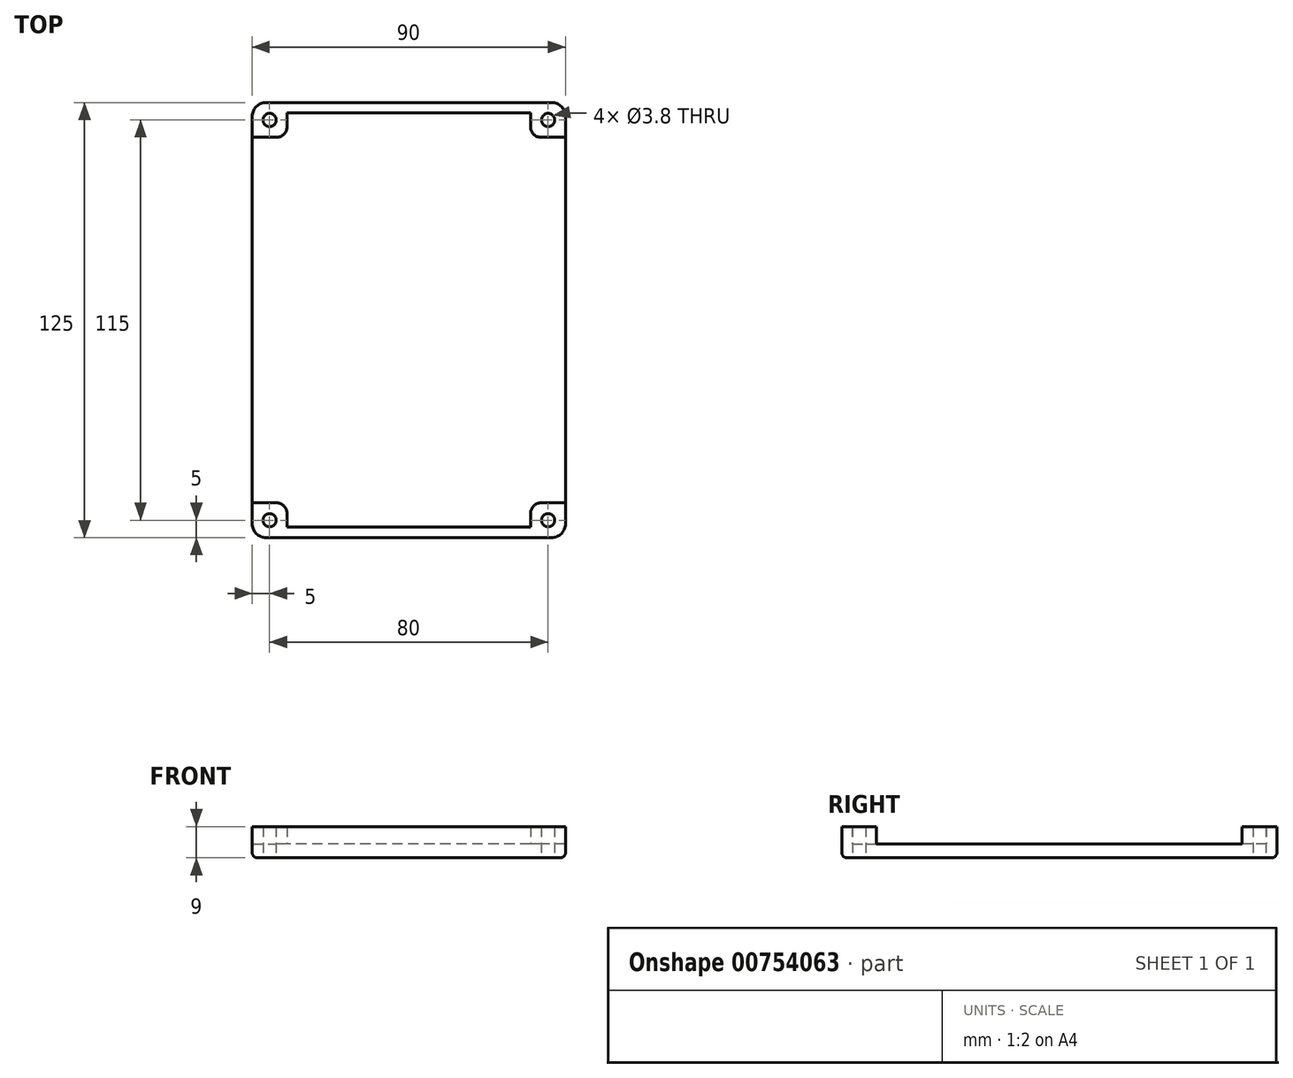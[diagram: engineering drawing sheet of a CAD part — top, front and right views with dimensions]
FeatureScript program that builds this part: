
annotation { "Feature Type Name" : "Feature", "Feature Type Description" : "" }
export const myFeature = defineFeature(function(context is Context, id is Id, definition is map)
    precondition{}
    {
        {
            var Q0;
            Q0=qCreatedBy(makeId("Top.planeOp"),FACE);
            var sketch = newSketch(context, id + "F0", { "sketchPlane" : qUnion([Q0])});
            skLineSegment(sketch, "E0.bottom", {"start": v(-41, 62.5) * mm, "end": v(41, 62.5) * mm});
            skLineSegment(sketch, "E0.top", {"start": v(-41, -62.5) * mm, "end": v(41, -62.5) * mm});
            skLineSegment(sketch, "E0.left", {"start": v(-45, 58.5) * mm, "end": v(-45, -58.5) * mm});
            skLineSegment(sketch, "E0.right", {"start": v(45, 58.5) * mm, "end": v(45, -58.5) * mm});
            skPoint(sketch, "E1.visualSharp", {"position": v(-45, 62.5) * mm});
            skArc(sketch, "E1.filletArc", {"start": v(-41, 62.5) * mm, "mid": v(-43.83, 61.33) * mm, "end": v(-45, 58.5) * mm});
            skPoint(sketch, "E2.visualSharp", {"position": v(45, 62.5) * mm});
            skArc(sketch, "E2.filletArc", {"start": v(45, 58.5) * mm, "mid": v(43.83, 61.33) * mm, "end": v(41, 62.5) * mm});
            skPoint(sketch, "E3.visualSharp", {"position": v(45, -62.5) * mm});
            skArc(sketch, "E3.filletArc", {"start": v(41, -62.5) * mm, "mid": v(43.83, -61.33) * mm, "end": v(45, -58.5) * mm});
            skPoint(sketch, "E4.visualSharp", {"position": v(-45, -62.5) * mm});
            skArc(sketch, "E4.filletArc", {"start": v(-45, -58.5) * mm, "mid": v(-43.83, -61.33) * mm, "end": v(-41, -62.5) * mm});
            skSolve(sketch);
        }
        {
            var Q0;
            Q0 = qSketchRegion(id + "F0", true);
            extrude(context, id + "F1", {"entities" : qUnion([Q0]), "depth" : 4 * mm, "offsetDistance" : 25 * mm});
        }
        {
            var Q0;
            Q0=makeQuery(id+"F1.opExtrude","CAP_FACE",FACE,{"disambiguationData":[OSD([sQuery(id+"F0.wireOp",EDGE,"E0.bottom"),sQuery(id+"F0.wireOp",EDGE,"E0.top"),sQuery(id+"F0.wireOp",EDGE,"E0.left"),sQuery(id+"F0.wireOp",EDGE,"E0.right"),sQuery(id+"F0.wireOp",EDGE,"E1.filletArc"),sQuery(id+"F0.wireOp",EDGE,"E2.filletArc"),sQuery(id+"F0.wireOp",EDGE,"E3.filletArc"),sQuery(id+"F0.wireOp",EDGE,"E4.filletArc")])],"isStart":false});
            var sketch = newSketch(context, id + "F2", { "sketchPlane" : qUnion([Q0])});
            skLineSegment(sketch, "E5.bottom", {"start": v(-41, 62.5) * mm, "end": v(-45, 62.5) * mm, "construction": true});
            skLineSegment(sketch, "E5.top", {"start": v(-41, 58.5) * mm, "end": v(-45, 58.5) * mm, "construction": true});
            skLineSegment(sketch, "E5.left", {"start": v(-41, 62.5) * mm, "end": v(-41, 58.5) * mm, "construction": true});
            skLineSegment(sketch, "E5.right", {"start": v(-45, 62.5) * mm, "end": v(-45, 58.5) * mm, "construction": true});
            skLineSegment(sketch, "E6.bottom", {"start": v(-45, 62.5) * mm, "end": v(-35, 62.5) * mm, "construction": true});
            skLineSegment(sketch, "E6.top", {"start": v(-45, 52.5) * mm, "end": v(-38, 52.5) * mm});
            skLineSegment(sketch, "E6.left", {"start": v(-45, 62.5) * mm, "end": v(-45, 52.5) * mm, "construction": true});
            skLineSegment(sketch, "E6.right", {"start": v(-35, 62.5) * mm, "end": v(-35, 55.5) * mm});
            skPoint(sketch, "E7.visualSharp", {"position": v(-35, 52.5) * mm});
            skArc(sketch, "E7.filletArc", {"start": v(-38, 52.5) * mm, "mid": v(-35.88, 53.38) * mm, "end": v(-35, 55.5) * mm});
            skLineSegment(sketch, "E8.bottom", {"start": v(41, 62.5) * mm, "end": v(45, 62.5) * mm, "construction": true});
            skLineSegment(sketch, "E8.top", {"start": v(41, 58.5) * mm, "end": v(45, 58.5) * mm, "construction": true});
            skLineSegment(sketch, "E8.left", {"start": v(41, 62.5) * mm, "end": v(41, 58.5) * mm, "construction": true});
            skLineSegment(sketch, "E8.right", {"start": v(45, 62.5) * mm, "end": v(45, 58.5) * mm, "construction": true});
            skLineSegment(sketch, "E9.bottom", {"start": v(45, 62.5) * mm, "end": v(35, 62.5) * mm, "construction": true});
            skLineSegment(sketch, "E9.top", {"start": v(45, 52.5) * mm, "end": v(38, 52.5) * mm});
            skLineSegment(sketch, "E9.left", {"start": v(45, 62.5) * mm, "end": v(45, 52.5) * mm});
            skLineSegment(sketch, "E9.right", {"start": v(35, 62.5) * mm, "end": v(35, 55.5) * mm});
            skPoint(sketch, "E10.visualSharp", {"position": v(35, 52.5) * mm});
            skArc(sketch, "E10.filletArc", {"start": v(35, 55.5) * mm, "mid": v(35.88, 53.38) * mm, "end": v(38, 52.5) * mm});
            skLineSegment(sketch, "E11.bottom", {"start": v(-35, 62.5) * mm, "end": v(35, 62.5) * mm});
            skLineSegment(sketch, "E11.top", {"start": v(-35, 59.5) * mm, "end": v(35, 59.5) * mm});
            skLineSegment(sketch, "E11.left", {"start": v(-35, 62.5) * mm, "end": v(-35, 59.5) * mm});
            skLineSegment(sketch, "E11.right", {"start": v(35, 62.5) * mm, "end": v(35, 59.5) * mm});
            skLineSegment(sketch, "E12.bottom", {"start": v(41, -62.5) * mm, "end": v(45, -62.5) * mm, "construction": true});
            skLineSegment(sketch, "E12.top", {"start": v(41, -58.5) * mm, "end": v(45, -58.5) * mm, "construction": true});
            skLineSegment(sketch, "E12.left", {"start": v(41, -62.5) * mm, "end": v(41, -58.5) * mm, "construction": true});
            skLineSegment(sketch, "E12.right", {"start": v(45, -62.5) * mm, "end": v(45, -58.5) * mm, "construction": true});
            skLineSegment(sketch, "E13.bottom", {"start": v(45, -62.5) * mm, "end": v(35, -62.5) * mm, "construction": true});
            skLineSegment(sketch, "E13.top", {"start": v(45, -52.5) * mm, "end": v(38, -52.5) * mm});
            skLineSegment(sketch, "E13.left", {"start": v(45, -62.5) * mm, "end": v(45, -52.5) * mm, "construction": true});
            skLineSegment(sketch, "E13.right", {"start": v(35, -62.5) * mm, "end": v(35, -55.5) * mm});
            skPoint(sketch, "E14.visualSharp", {"position": v(35, -52.5) * mm});
            skArc(sketch, "E14.filletArc", {"start": v(38, -52.5) * mm, "mid": v(35.88, -53.38) * mm, "end": v(35, -55.5) * mm});
            skLineSegment(sketch, "E15.bottom", {"start": v(45, 52.5) * mm, "end": v(42, 52.5) * mm});
            skLineSegment(sketch, "E15.top", {"start": v(45, -52.5) * mm, "end": v(42, -52.5) * mm});
            skLineSegment(sketch, "E15.left", {"start": v(45, 52.5) * mm, "end": v(45, -52.5) * mm});
            skLineSegment(sketch, "E15.right", {"start": v(42, 52.5) * mm, "end": v(42, -52.5) * mm});
            skLineSegment(sketch, "E16.bottom", {"start": v(-45, -58.5) * mm, "end": v(-41, -58.5) * mm, "construction": true});
            skLineSegment(sketch, "E16.top", {"start": v(-45, -62.5) * mm, "end": v(-41, -62.5) * mm, "construction": true});
            skLineSegment(sketch, "E16.left", {"start": v(-45, -58.5) * mm, "end": v(-45, -62.5) * mm, "construction": true});
            skLineSegment(sketch, "E16.right", {"start": v(-41, -58.5) * mm, "end": v(-41, -62.5) * mm, "construction": true});
            skLineSegment(sketch, "E17.bottom", {"start": v(-45, -62.5) * mm, "end": v(-35, -62.5) * mm, "construction": true});
            skLineSegment(sketch, "E17.top", {"start": v(-45, -52.5) * mm, "end": v(-38, -52.5) * mm});
            skLineSegment(sketch, "E17.left", {"start": v(-45, -62.5) * mm, "end": v(-45, -52.5) * mm, "construction": true});
            skLineSegment(sketch, "E17.right", {"start": v(-35, -62.5) * mm, "end": v(-35, -55.5) * mm});
            skPoint(sketch, "E18.visualSharp", {"position": v(-35, -52.5) * mm});
            skArc(sketch, "E18.filletArc", {"start": v(-35, -55.5) * mm, "mid": v(-35.88, -53.38) * mm, "end": v(-38, -52.5) * mm});
            skLineSegment(sketch, "E19.bottom", {"start": v(35, -62.5) * mm, "end": v(-35, -62.5) * mm});
            skLineSegment(sketch, "E19.top", {"start": v(35, -59.5) * mm, "end": v(-35, -59.5) * mm});
            skLineSegment(sketch, "E19.left", {"start": v(35, -62.5) * mm, "end": v(35, -59.5) * mm});
            skLineSegment(sketch, "E19.right", {"start": v(-35, -62.5) * mm, "end": v(-35, -59.5) * mm});
            skLineSegment(sketch, "E20.bottom", {"start": v(-45, 52.5) * mm, "end": v(-42, 52.5) * mm});
            skLineSegment(sketch, "E20.top", {"start": v(-45, -52.5) * mm, "end": v(-42, -52.5) * mm});
            skLineSegment(sketch, "E20.left", {"start": v(-45, 52.5) * mm, "end": v(-45, -52.5) * mm});
            skLineSegment(sketch, "E20.right", {"start": v(-42, 52.5) * mm, "end": v(-42, -52.5) * mm});
            skLineSegment(sketch, "E21.bottom", {"start": v(-35, 52.5) * mm, "end": v(-45, 52.5) * mm, "construction": true});
            skLineSegment(sketch, "E21.top", {"start": v(-35, 62.5) * mm, "end": v(-45, 62.5) * mm, "construction": true});
            skLineSegment(sketch, "E21.left", {"start": v(-35, 52.5) * mm, "end": v(-35, 62.5) * mm, "construction": true});
            skLineSegment(sketch, "E21.right", {"start": v(-45, 52.5) * mm, "end": v(-45, 62.5) * mm, "construction": true});
            skLineSegment(sketch, "E22", {"start": v(-40, 52.5) * mm, "end": v(-40, 62.5) * mm, "construction": true});
            skLineSegment(sketch, "E23", {"start": v(-35, 57.5) * mm, "end": v(-45, 57.5) * mm, "construction": true});
            skCircle(sketch, "E24", {"center": v(-40, 57.5) * mm, "radius": 1.9 * mm});
            skLineSegment(sketch, "E25.top", {"start": v(45, 52.5) * mm, "end": v(35, 52.5) * mm, "construction": true});
            skLineSegment(sketch, "E25.left", {"start": v(45, 62.5) * mm, "end": v(45, 52.5) * mm, "construction": true});
            skLineSegment(sketch, "E25.right", {"start": v(35, 62.5) * mm, "end": v(35, 52.5) * mm, "construction": true});
            skLineSegment(sketch, "E26", {"start": v(40, 62.5) * mm, "end": v(40, 52.5) * mm, "construction": true});
            skLineSegment(sketch, "E27", {"start": v(35, 57.5) * mm, "end": v(45, 57.5) * mm, "construction": true});
            skCircle(sketch, "E28", {"center": v(40, 57.5) * mm, "radius": 1.9 * mm});
            skLineSegment(sketch, "E29.top", {"start": v(45, -52.5) * mm, "end": v(35, -52.5) * mm, "construction": true});
            skLineSegment(sketch, "E29.right", {"start": v(35, -62.5) * mm, "end": v(35, -52.5) * mm, "construction": true});
            skLineSegment(sketch, "E30", {"start": v(40, -52.5) * mm, "end": v(40, -62.5) * mm, "construction": true});
            skLineSegment(sketch, "E31", {"start": v(45, -57.5) * mm, "end": v(35, -57.5) * mm, "construction": true});
            skCircle(sketch, "E32", {"center": v(40, -57.5) * mm, "radius": 1.9 * mm});
            skLineSegment(sketch, "E33.top", {"start": v(-45, -52.5) * mm, "end": v(-35, -52.5) * mm, "construction": true});
            skLineSegment(sketch, "E33.right", {"start": v(-35, -62.5) * mm, "end": v(-35, -52.5) * mm, "construction": true});
            skLineSegment(sketch, "E34", {"start": v(-40, -52.5) * mm, "end": v(-40, -62.5) * mm, "construction": true});
            skLineSegment(sketch, "E35", {"start": v(-35, -57.5) * mm, "end": v(-45, -57.5) * mm, "construction": true});
            skCircle(sketch, "E36", {"center": v(-40, -57.5) * mm, "radius": 1.9 * mm});
            skSolve(sketch);
        }
        {
            var Q0;
            Q0=makeQuery(id+"F2.imprint","IMPRINT",FACE,{"disambiguationData":[TD([[makeQuery(id+"F2.imprint","IMPRINT",EDGE,{"derivedFrom":sQuery(id+"F2.wireOp",EDGE,"E15.bottom")}),1.0]])]});
            var Q1;
            Q1=makeQuery(id+"F2.imprint","IMPRINT",FACE,{"disambiguationData":[TD([[makeQuery(id+"F2.imprint","IMPRINT",EDGE,{"derivedFrom":sQuery(id+"F2.wireOp",EDGE,"E19.bottom")}),1.0]])]});
            var Q2;
            Q2=makeQuery(id+"F2.imprint","IMPRINT",FACE,{"disambiguationData":[TD([[makeQuery(id+"F2.imprint","IMPRINT",EDGE,{"derivedFrom":sQuery(id+"F2.wireOp",EDGE,"E20.bottom")}),-1.0]])]});
            var Q3;
            Q3=makeQuery(id+"F2.imprint","IMPRINT",FACE,{"disambiguationData":[TD([[makeQuery(id+"F2.imprint","IMPRINT",EDGE,{"derivedFrom":sQuery(id+"F2.wireOp",EDGE,"E11.top")}),1.0]])]});
            var Q4;
            Q4=makeQuery(id+"F2.imprint","IMPRINT",FACE,{"disambiguationData":[TD([[makeQuery(id+"F2.imprint","IMPRINT",EDGE,{"derivedFrom":sQuery(id+"F2.wireOp",EDGE,"E6.top")}),1.0]])]});
            var Q5;
            Q5=makeQuery(id+"F2.imprint","IMPRINT",FACE,{"disambiguationData":[TD([[makeQuery(id+"F2.imprint","IMPRINT",EDGE,{"derivedFrom":sQuery(id+"F2.wireOp",EDGE,"E9.top")}),-1.0]])]});
            var Q6;
            Q6=makeQuery(id+"F2.imprint","IMPRINT",FACE,{"disambiguationData":[TD([[makeQuery(id+"F2.imprint","IMPRINT",EDGE,{"derivedFrom":sQuery(id+"F2.wireOp",EDGE,"E13.top")}),1.0]])]});
            var Q7;
            Q7=makeQuery(id+"F2.imprint","IMPRINT",FACE,{"disambiguationData":[TD([[makeQuery(id+"F2.imprint","IMPRINT",EDGE,{"derivedFrom":sQuery(id+"F2.wireOp",EDGE,"E17.top")}),-1.0]])]});
            extrude(context, id + "F3", {"entities" : qUnion([Q0, Q1, Q2, Q3, Q4, Q5, Q6, Q7]), "operationType" : NewBodyOperationType.ADD, "depth" : 5 * mm, "offsetDistance" : 25 * mm});
        }
        {
            var Q0;
            Q0=makeQuery(id+"F1.opExtrude","CAP_FACE",FACE,{"disambiguationData":[OSD([sQuery(id+"F0.wireOp",EDGE,"E0.bottom"),sQuery(id+"F0.wireOp",EDGE,"E0.top"),sQuery(id+"F0.wireOp",EDGE,"E0.left"),sQuery(id+"F0.wireOp",EDGE,"E0.right"),sQuery(id+"F0.wireOp",EDGE,"E1.filletArc"),sQuery(id+"F0.wireOp",EDGE,"E2.filletArc"),sQuery(id+"F0.wireOp",EDGE,"E3.filletArc"),sQuery(id+"F0.wireOp",EDGE,"E4.filletArc")])],"isStart":true});
            fillet(context, id + "F4", {"entities" : qUnion([Q0]), "radius" : 1.5 * mm, "tangentPropagation" : true, "allowEdgeOverflow" : false});
        }
        {
            var Q0;
            Q0=makeQuery(id+"F3.boolean.opBoolean","SPLIT",FACE,{"disambiguationData":[TD([makeQuery(id+"F3.opExtrude","SWEPT_FACE",FACE,{"disambiguationData":[OSD([sQuery(id+"F2.wireOp",EDGE,"E24")])]})])],"derivedFrom":makeQuery(id+"F1.opExtrude","CAP_FACE",FACE,{"disambiguationData":[OSD([sQuery(id+"F0.wireOp",EDGE,"E0.bottom"),sQuery(id+"F0.wireOp",EDGE,"E0.top"),sQuery(id+"F0.wireOp",EDGE,"E0.left"),sQuery(id+"F0.wireOp",EDGE,"E0.right"),sQuery(id+"F0.wireOp",EDGE,"E1.filletArc"),sQuery(id+"F0.wireOp",EDGE,"E2.filletArc"),sQuery(id+"F0.wireOp",EDGE,"E3.filletArc"),sQuery(id+"F0.wireOp",EDGE,"E4.filletArc")])],"isStart":false})});
            extrude(context, id + "F5", {"entities" : qUnion([Q0]), "operationType" : NewBodyOperationType.REMOVE, "oppositeDirection" : true, "depth" : 25 * mm, "offsetDistance" : 25 * mm});
        }
        {
            var Q0;
            Q0=makeQuery(id+"F3.boolean.opBoolean","SPLIT",FACE,{"disambiguationData":[TD([makeQuery(id+"F3.opExtrude","SWEPT_FACE",FACE,{"disambiguationData":[OSD([sQuery(id+"F2.wireOp",EDGE,"E28")])]})])],"derivedFrom":makeQuery(id+"F1.opExtrude","CAP_FACE",FACE,{"disambiguationData":[OSD([sQuery(id+"F0.wireOp",EDGE,"E0.bottom"),sQuery(id+"F0.wireOp",EDGE,"E0.top"),sQuery(id+"F0.wireOp",EDGE,"E0.left"),sQuery(id+"F0.wireOp",EDGE,"E0.right"),sQuery(id+"F0.wireOp",EDGE,"E1.filletArc"),sQuery(id+"F0.wireOp",EDGE,"E2.filletArc"),sQuery(id+"F0.wireOp",EDGE,"E3.filletArc"),sQuery(id+"F0.wireOp",EDGE,"E4.filletArc")])],"isStart":false})});
            extrude(context, id + "F6", {"entities" : qUnion([Q0]), "operationType" : NewBodyOperationType.REMOVE, "oppositeDirection" : true, "depth" : 25 * mm, "offsetDistance" : 25 * mm});
        }
        {
            var Q0;
            Q0=makeQuery(id+"F3.boolean.opBoolean","SPLIT",FACE,{"disambiguationData":[TD([makeQuery(id+"F3.opExtrude","SWEPT_FACE",FACE,{"disambiguationData":[OSD([sQuery(id+"F2.wireOp",EDGE,"E32")])]})])],"derivedFrom":makeQuery(id+"F1.opExtrude","CAP_FACE",FACE,{"disambiguationData":[OSD([sQuery(id+"F0.wireOp",EDGE,"E0.bottom"),sQuery(id+"F0.wireOp",EDGE,"E0.top"),sQuery(id+"F0.wireOp",EDGE,"E0.left"),sQuery(id+"F0.wireOp",EDGE,"E0.right"),sQuery(id+"F0.wireOp",EDGE,"E1.filletArc"),sQuery(id+"F0.wireOp",EDGE,"E2.filletArc"),sQuery(id+"F0.wireOp",EDGE,"E3.filletArc"),sQuery(id+"F0.wireOp",EDGE,"E4.filletArc")])],"isStart":false})});
            extrude(context, id + "F7", {"entities" : qUnion([Q0]), "operationType" : NewBodyOperationType.REMOVE, "oppositeDirection" : true, "depth" : 25 * mm, "offsetDistance" : 25 * mm});
        }
        {
            var Q0;
            Q0=makeQuery(id+"F3.boolean.opBoolean","SPLIT",FACE,{"disambiguationData":[TD([makeQuery(id+"F3.opExtrude","SWEPT_FACE",FACE,{"disambiguationData":[OSD([sQuery(id+"F2.wireOp",EDGE,"E36")])]})])],"derivedFrom":makeQuery(id+"F1.opExtrude","CAP_FACE",FACE,{"disambiguationData":[OSD([sQuery(id+"F0.wireOp",EDGE,"E0.bottom"),sQuery(id+"F0.wireOp",EDGE,"E0.top"),sQuery(id+"F0.wireOp",EDGE,"E0.left"),sQuery(id+"F0.wireOp",EDGE,"E0.right"),sQuery(id+"F0.wireOp",EDGE,"E1.filletArc"),sQuery(id+"F0.wireOp",EDGE,"E2.filletArc"),sQuery(id+"F0.wireOp",EDGE,"E3.filletArc"),sQuery(id+"F0.wireOp",EDGE,"E4.filletArc")])],"isStart":false})});
            extrude(context, id + "F8", {"entities" : qUnion([Q0]), "operationType" : NewBodyOperationType.REMOVE, "oppositeDirection" : true, "depth" : 25 * mm, "offsetDistance" : 25 * mm});
        }
    });
